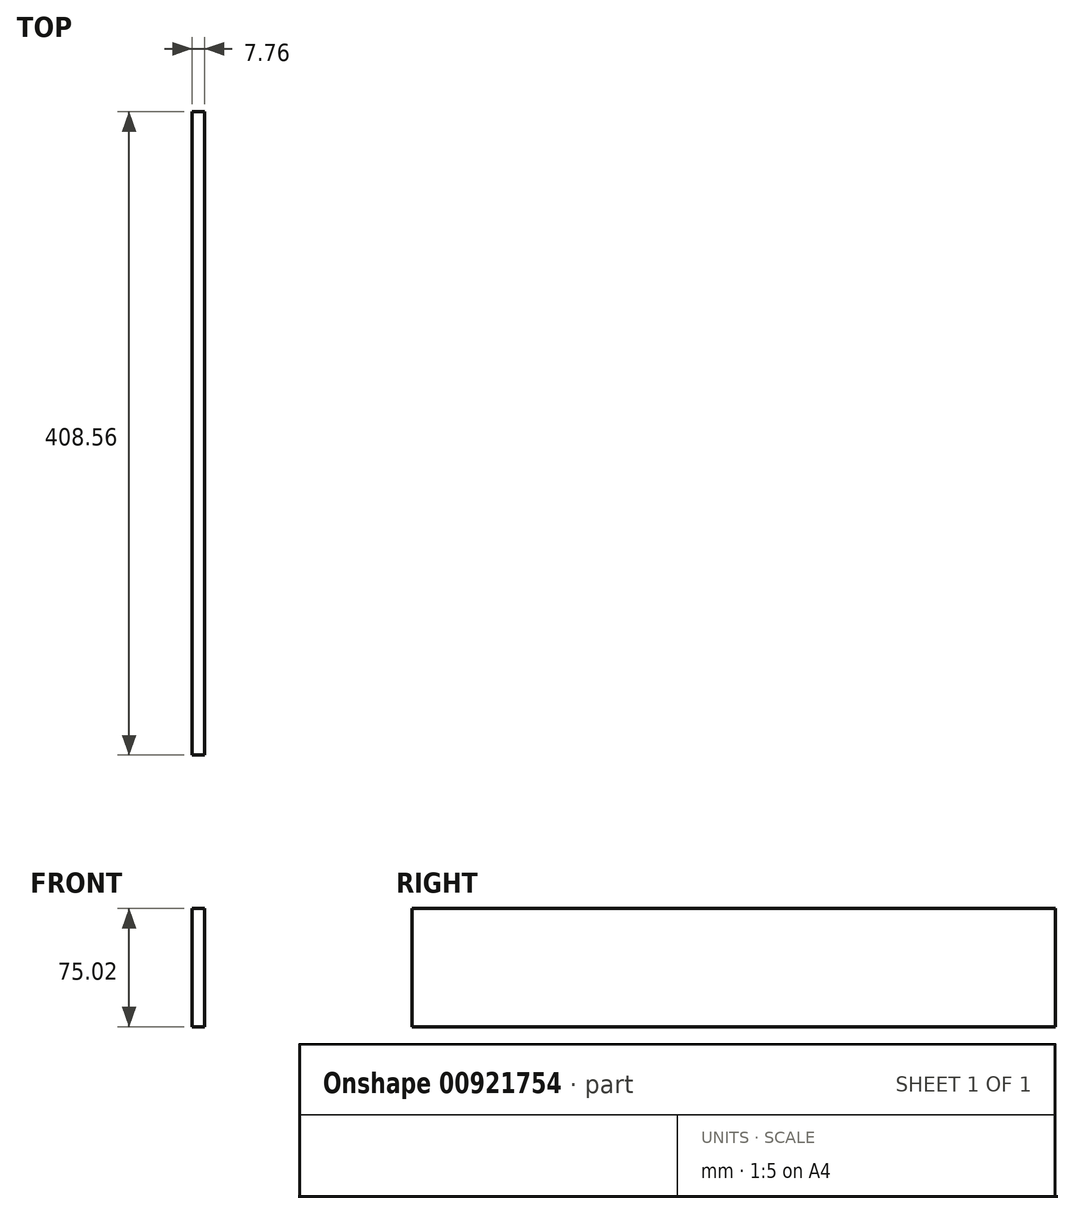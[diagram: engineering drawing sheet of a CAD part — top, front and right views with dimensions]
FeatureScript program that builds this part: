
annotation { "Feature Type Name" : "Feature", "Feature Type Description" : "" }
export const myFeature = defineFeature(function(context is Context, id is Id, definition is map)
    precondition{}
    {
        {
            var Q0;
            Q0=qCreatedBy(makeId("Front.planeOp"),FACE);
            var sketch = newSketch(context, id + "F0", { "sketchPlane" : qUnion([Q0])});
            skLineSegment(sketch, "E0.bottom", {"start": v(-53.58, 46.93) * mm, "end": v(-45.82, 46.93) * mm});
            skLineSegment(sketch, "E0.top", {"start": v(-53.58, -28.09) * mm, "end": v(-45.82, -28.09) * mm});
            skLineSegment(sketch, "E0.left", {"start": v(-53.58, 46.93) * mm, "end": v(-53.58, -28.09) * mm});
            skLineSegment(sketch, "E0.right", {"start": v(-45.82, 46.93) * mm, "end": v(-45.82, -28.09) * mm});
            skSolve(sketch);
        }
        {
            var Q0;
            Q0 = qSketchRegion(id + "F0", true);
            extrude(context, id + "F1", {"entities" : qUnion([Q0]), "depth" : 408.56 * mm, "offsetDistance" : 25.4 * mm});
        }
    });
